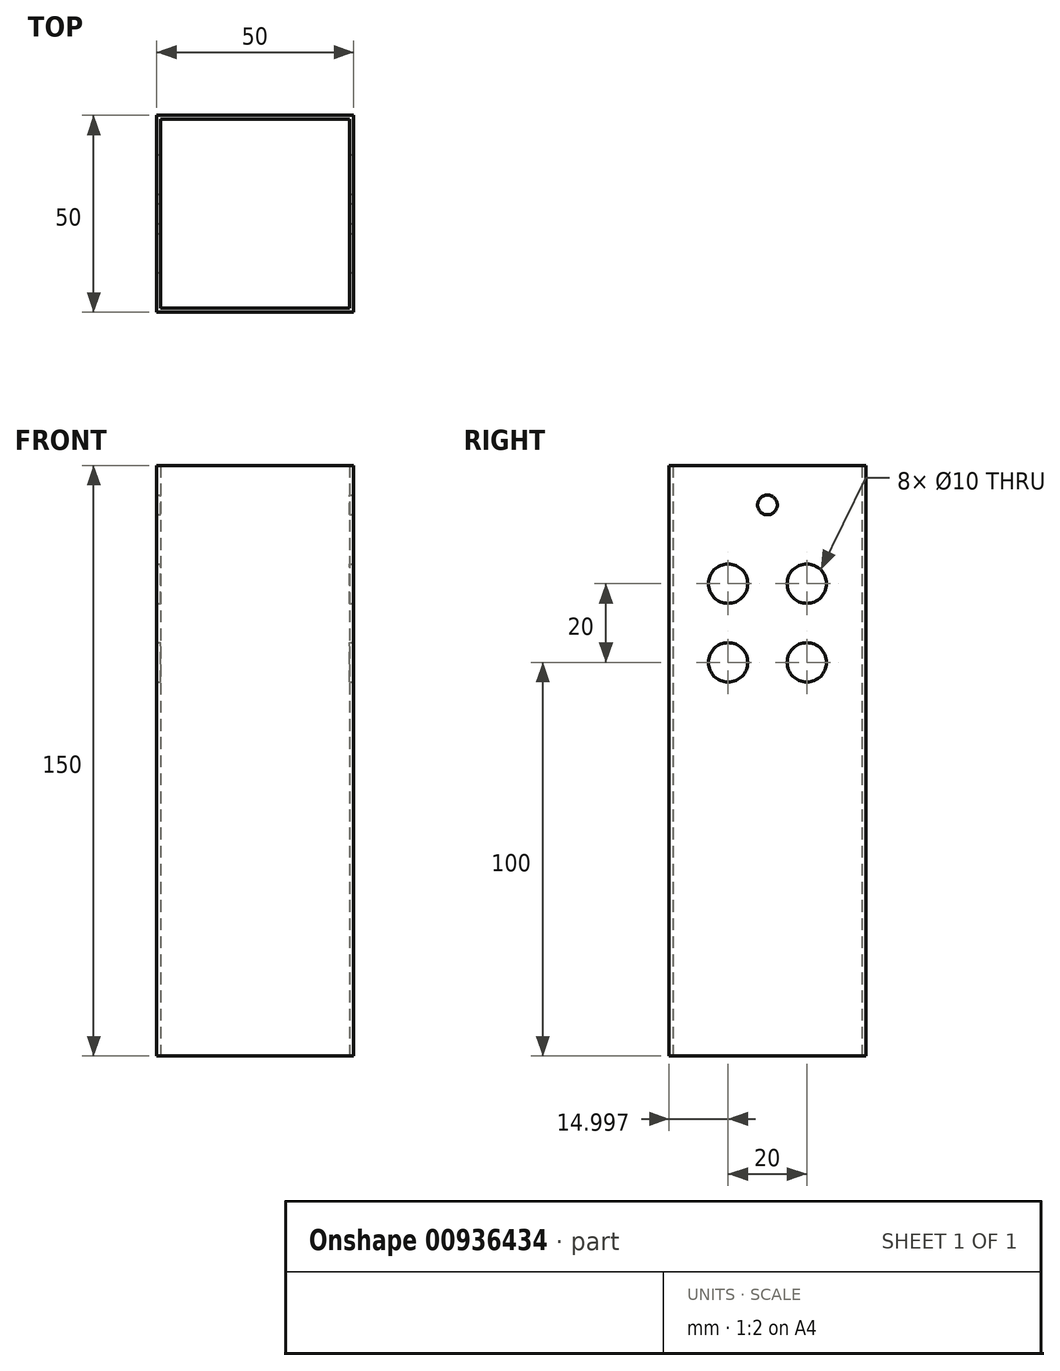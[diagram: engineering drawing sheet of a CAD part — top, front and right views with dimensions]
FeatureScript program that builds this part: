
annotation { "Feature Type Name" : "Feature", "Feature Type Description" : "" }
export const myFeature = defineFeature(function(context is Context, id is Id, definition is map)
    precondition{}
    {
        {
            var Q0;
            Q0=qCreatedBy(makeId("Top.planeOp"),FACE);
            var sketch = newSketch(context, id + "F0", { "sketchPlane" : qUnion([Q0])});
            skLineSegment(sketch, "E0.bottom", {"start": v(0, 16.92) * mm, "end": v(50, 16.92) * mm});
            skLineSegment(sketch, "E0.top", {"start": v(0, -33.08) * mm, "end": v(50, -33.08) * mm});
            skLineSegment(sketch, "E0.left", {"start": v(0, 16.92) * mm, "end": v(0, -33.08) * mm});
            skLineSegment(sketch, "E0.right", {"start": v(50, 16.92) * mm, "end": v(50, -33.08) * mm});
            skLineSegment(sketch, "E1.bottom", {"start": v(1, 15.92) * mm, "end": v(49, 15.92) * mm});
            skLineSegment(sketch, "E1.top", {"start": v(1, -32.08) * mm, "end": v(49, -32.08) * mm});
            skLineSegment(sketch, "E1.left", {"start": v(1, 15.92) * mm, "end": v(1, -32.08) * mm});
            skLineSegment(sketch, "E1.right", {"start": v(49, 15.92) * mm, "end": v(49, -32.08) * mm});
            skSolve(sketch);
        }
        {
            var Q0;
            Q0 = qSketchRegion(id + "F0", true);
            extrude(context, id + "F1", {"entities" : qUnion([Q0]), "depth" : 150 * mm, "offsetDistance" : 25 * mm});
        }
        {
            var Q0;
            Q0=makeQuery(id+"F1.opExtrude","SWEPT_FACE",FACE,{"disambiguationData":[OSD([sQuery(id+"F0.wireOp",EDGE,"E0.right")])]});
            var sketch = newSketch(context, id + "F2", { "sketchPlane" : qUnion([Q0])});
            skLineSegment(sketch, "E2.bottom", {"start": v(-33.08, 150) * mm, "end": v(-18.08, 150) * mm});
            skLineSegment(sketch, "E2.top", {"start": v(-33.08, 120) * mm, "end": v(-18.08, 120) * mm});
            skLineSegment(sketch, "E2.left", {"start": v(-33.08, 150) * mm, "end": v(-33.08, 120) * mm});
            skLineSegment(sketch, "E2.right", {"start": v(-18.08, 150) * mm, "end": v(-18.08, 120) * mm});
            skLineSegment(sketch, "E3.bottom", {"start": v(-18.08, 120) * mm, "end": v(1.92, 120) * mm});
            skLineSegment(sketch, "E3.top", {"start": v(-18.08, 100) * mm, "end": v(1.92, 100) * mm});
            skLineSegment(sketch, "E3.left", {"start": v(-18.08, 120) * mm, "end": v(-18.08, 100) * mm});
            skLineSegment(sketch, "E3.right", {"start": v(1.92, 120) * mm, "end": v(1.92, 100) * mm});
            skCircle(sketch, "E4", {"center": v(-18.08, 120) * mm, "radius": 5 * mm});
            skCircle(sketch, "E5", {"center": v(1.92, 120) * mm, "radius": 5 * mm});
            skCircle(sketch, "E6", {"center": v(1.92, 100) * mm, "radius": 5 * mm});
            skCircle(sketch, "E7", {"center": v(-18.08, 100) * mm, "radius": 5 * mm});
            skCircle(sketch, "E8", {"center": v(-8.08, 140) * mm, "radius": 2.5 * mm});
            skPoint(sketch, "E8.centerSnap0", {"position": v(-8.08, 120) * mm});
            skSolve(sketch);
        }
        {
            var Q0;
            Q0=makeQuery(id+"F2.imprint","IMPRINT",FACE,{"disambiguationData":[TD([[makeQuery(id+"F2.imprint","IMPRINT",EDGE,{"derivedFrom":sQuery(id+"F2.wireOp",EDGE,"E8")}),1.0]])]});
            var Q1;
            {var subQ0=sQuery(id+"F2.wireOp",EDGE,"E3.right");var subQ1=sQuery(id+"F2.wireOp",EDGE,"E3.bottom");var subQ2=makeQuery(id+"F2.imprint","INTERSECT",VERTEX,{"derivedFrom":[subQ1,subQ0]});Q1=makeQuery(id+"F2.imprint","IMPRINT",FACE,{"disambiguationData":[TD([[makeQuery(id+"F2.imprint","IMPRINT",EDGE,{"disambiguationData":[TD([[subQ2,1.0]])],"derivedFrom":subQ1}),-1.0]])]});}
            var Q2;
            {var subQ0=sQuery(id+"F2.wireOp",EDGE,"E3.right");var subQ1=sQuery(id+"F2.wireOp",EDGE,"E3.bottom");var subQ2=makeQuery(id+"F2.imprint","INTERSECT",VERTEX,{"derivedFrom":[subQ1,subQ0]});Q2=makeQuery(id+"F2.imprint","IMPRINT",FACE,{"disambiguationData":[TD([[makeQuery(id+"F2.imprint","IMPRINT",EDGE,{"disambiguationData":[TD([[subQ2,1.0]])],"derivedFrom":subQ1}),1.0]])]});}
            var Q3;
            {var subQ0=sQuery(id+"F2.wireOp",EDGE,"E3.left");var subQ1=sQuery(id+"F2.wireOp",EDGE,"E3.top");var subQ2=makeQuery(id+"F2.imprint","INTERSECT",VERTEX,{"derivedFrom":[subQ1,subQ0]});Q3=makeQuery(id+"F2.imprint","IMPRINT",FACE,{"disambiguationData":[TD([[makeQuery(id+"F2.imprint","IMPRINT",EDGE,{"disambiguationData":[TD([[subQ2,-1.0]])],"derivedFrom":subQ1}),1.0]])]});}
            var Q4;
            {var subQ0=sQuery(id+"F2.wireOp",EDGE,"E3.left");var subQ1=sQuery(id+"F2.wireOp",EDGE,"E3.top");var subQ2=makeQuery(id+"F2.imprint","INTERSECT",VERTEX,{"derivedFrom":[subQ1,subQ0]});Q4=makeQuery(id+"F2.imprint","IMPRINT",FACE,{"disambiguationData":[TD([[makeQuery(id+"F2.imprint","IMPRINT",EDGE,{"disambiguationData":[TD([[subQ2,-1.0]])],"derivedFrom":subQ1}),-1.0]])]});}
            var Q5;
            {var subQ0=sQuery(id+"F2.wireOp",EDGE,"E3.right");var subQ1=sQuery(id+"F2.wireOp",EDGE,"E3.top");var subQ2=makeQuery(id+"F2.imprint","INTERSECT",VERTEX,{"derivedFrom":[subQ1,subQ0]});Q5=makeQuery(id+"F2.imprint","IMPRINT",FACE,{"disambiguationData":[TD([[makeQuery(id+"F2.imprint","IMPRINT",EDGE,{"disambiguationData":[TD([[subQ2,1.0]])],"derivedFrom":subQ1}),1.0]])]});}
            var Q6;
            {var subQ0=sQuery(id+"F2.wireOp",EDGE,"E3.right");var subQ1=sQuery(id+"F2.wireOp",EDGE,"E3.top");var subQ2=makeQuery(id+"F2.imprint","INTERSECT",VERTEX,{"derivedFrom":[subQ1,subQ0]});Q6=makeQuery(id+"F2.imprint","IMPRINT",FACE,{"disambiguationData":[TD([[makeQuery(id+"F2.imprint","IMPRINT",EDGE,{"disambiguationData":[TD([[subQ2,1.0]])],"derivedFrom":subQ1}),-1.0]])]});}
            var Q7;
            {var subQ1=sQuery(id+"F2.wireOp",EDGE,"E2.top");var subQ3=sQuery(id+"F2.wireOp",EDGE,"E4");var subQ4=makeQuery(id+"F2.imprint","INTERSECT",VERTEX,{"derivedFrom":[subQ1,subQ3]});Q7=makeQuery(id+"F2.imprint","IMPRINT",FACE,{"disambiguationData":[TD([[makeQuery(id+"F2.imprint","IMPRINT",EDGE,{"disambiguationData":[TD([[subQ4,1.0]])],"derivedFrom":subQ3}),1.0]])]});}
            var Q8;
            {var subQ1=sQuery(id+"F2.wireOp",EDGE,"E2.top");var subQ3=sQuery(id+"F2.wireOp",EDGE,"E4");var subQ4=makeQuery(id+"F2.imprint","INTERSECT",VERTEX,{"derivedFrom":[subQ1,subQ3]});Q8=makeQuery(id+"F2.imprint","IMPRINT",FACE,{"disambiguationData":[TD([[makeQuery(id+"F2.imprint","IMPRINT",EDGE,{"disambiguationData":[TD([[subQ4,-1.0]])],"derivedFrom":subQ3}),1.0]])]});}
            var Q9;
            {var subQ1=sQuery(id+"F2.wireOp",EDGE,"E2.right");var subQ3=sQuery(id+"F2.wireOp",EDGE,"E4");var subQ4=makeQuery(id+"F2.imprint","INTERSECT",VERTEX,{"derivedFrom":[subQ1,subQ3]});Q9=makeQuery(id+"F2.imprint","IMPRINT",FACE,{"disambiguationData":[TD([[makeQuery(id+"F2.imprint","IMPRINT",EDGE,{"disambiguationData":[TD([[subQ4,1.0]])],"derivedFrom":subQ3}),1.0]])]});}
            var Q10;
            {var subQ1=sQuery(id+"F2.wireOp",EDGE,"E3.bottom");var subQ3=sQuery(id+"F2.wireOp",EDGE,"E4");var subQ4=makeQuery(id+"F2.imprint","INTERSECT",VERTEX,{"derivedFrom":[subQ1,subQ3]});Q10=makeQuery(id+"F2.imprint","IMPRINT",FACE,{"disambiguationData":[TD([[makeQuery(id+"F2.imprint","IMPRINT",EDGE,{"disambiguationData":[TD([[subQ4,1.0]])],"derivedFrom":subQ3}),1.0]])]});}
            extrude(context, id + "F3", {"entities" : qUnion([Q0, Q1, Q2, Q3, Q4, Q5, Q6, Q7, Q8, Q9, Q10]), "operationType" : NewBodyOperationType.REMOVE, "oppositeDirection" : true, "depth" : 50 * mm, "offsetDistance" : 25 * mm});
        }
    });
